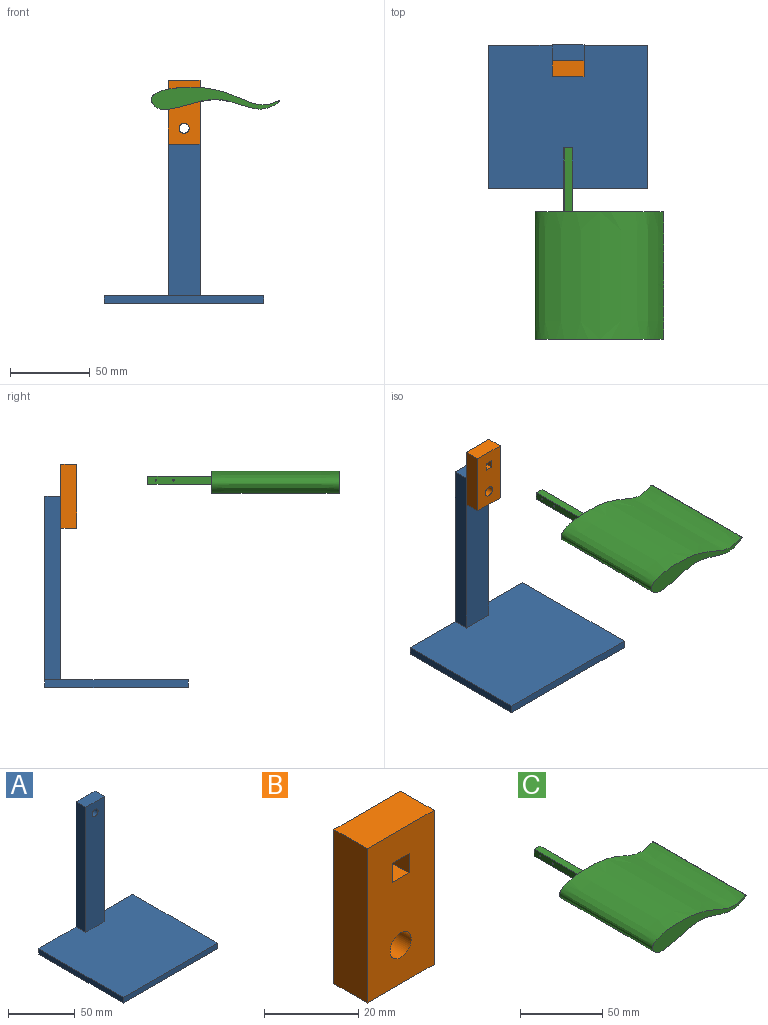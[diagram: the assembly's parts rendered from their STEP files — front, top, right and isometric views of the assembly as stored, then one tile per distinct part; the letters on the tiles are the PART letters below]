
ASSEMBLY  parts=3 mates=3
PART A: 11 faces, bbox 100x90x120 mm
  f0: plane 115x10mm, normal (-1,0,0), area 1150mm2, adj f3,f4,f5,f6
  f1: plane 100x90mm, normal (0,0,-1), area 9000mm2, adj f4,f7,f8,f9
  f2: plane 115x10mm, normal (1,0,0), area 1150mm2, adj f3,f4,f5,f6
  f3: plane 20x10mm, normal (0,0,1), area 200mm2, adj f0,f2,f4,f5
  f4: plane 120x100mm, normal (0,1,0), area 2768.3mm2, adj f0,f1,f2,f3,f6,f7,f8,f10
  f5: plane 115x20mm, normal (0,-1,0), area 2268.3mm2, adj f0,f2,f3,f6,f10
  f6: plane 100x90mm, normal (0,0,1), area 8800mm2, adj f0,f2,f4,f5,f7,f8,f9
  f7: plane 90x5mm, normal (-1,0,0), area 450mm2, adj f1,f4,f6,f9
  f8: plane 90x5mm, normal (1,0,0), area 450mm2, adj f1,f4,f6,f9
  f9: plane 100x5mm, normal (0,-1,0), area 500mm2, adj f1,f6,f7,f8
  f10: cylinder r=3.17mm len=10mm, axis (0,-1,0), area 199.5mm2, adj f4,f5
PART B: 11 faces, bbox 20x10x40 mm
  f0: plane 10x5mm, normal (-1,0,0), area 50mm2, adj f1,f7,f8,f9
  f1: plane 10x5mm, normal (0,0,1), area 50mm2, adj f0,f2,f8,f9
  f2: plane 10x5mm, normal (1,0,0), area 50mm2, adj f1,f7,f8,f9
  f3: plane 20x10mm, normal (0,0,-1), area 200mm2, adj f4,f6,f8,f9
  f4: plane 40x10mm, normal (1,0,0), area 400mm2, adj f3,f5,f8,f9
  f5: plane 20x10mm, normal (0,0,1), area 200mm2, adj f4,f6,f8,f9
  f6: plane 40x10mm, normal (-1,0,0), area 400mm2, adj f3,f5,f8,f9
  f7: plane 10x5mm, normal (0,0,-1), area 50mm2, adj f0,f2,f8,f9
  f8: plane 40x20mm, normal (0,-1,0), area 743.3mm2, adj f0,f1,f2,f3,f4,f5,f6,f7
  f9: plane 40x20mm, normal (0,1,0), area 743.3mm2, adj f0,f1,f2,f3,f4,f5,f6,f7
  f10: cylinder r=3.17mm len=10mm, axis (0,1,0), area 199.5mm2, adj f8,f9
PART C: 10 faces, bbox 84.1x120x17.4 mm
  f0: extruded ~80.22x80mm, area 13814.7mm2, adj f1,f2
  f1: plane 84.14x17.42mm, normal (0,-1,0), area 538.7mm2, adj f0
  f2: plane 84.14x17.42mm, normal (0,1,0), area 513.7mm2, adj f0,f3,f4,f5,f6
  f3: plane 40x5mm, normal (1,0,-0.03), area 198.4mm2, adj f2,f4,f6,f7,f8,f9
  f4: plane 40x5mm, normal (-0.03,0,-1), area 200mm2, adj f2,f3,f5,f7
  f5: plane 40x5mm, normal (-1,0,0.03), area 198.4mm2, adj f2,f4,f6,f7,f8,f9
  f6: plane 40x5mm, normal (0.03,0,1), area 200mm2, adj f2,f3,f5,f7
  f7: plane 5.15x5.15mm, normal (0,1,0), area 25mm2, adj f3,f4,f5,f6
  f8: cylinder r=0.5mm len=5.03mm, axis (-1,0,0.03), area 15.7mm2, adj f3,f5
  f9: cylinder r=0.5mm len=5.03mm, axis (-1,0,0.03), area 15.7mm2, adj f3,f5
PLACE A t=(0,-10,60)mm
PLACE B t=(0,-10,60)mm
PLACE C t=(19.92,-144.64,128.13)mm
MATE planar B.f10 <-> A.f10  axis (0,1,0) through (0,-10,110)mm
MATE slider C.f7 <-> B.f8  axis (0,1,0) through (0,-64.64,130)mm
MATE revolute B.f10 <-> A.f10  axis (0,1,0) through (0,-10,110)mm
